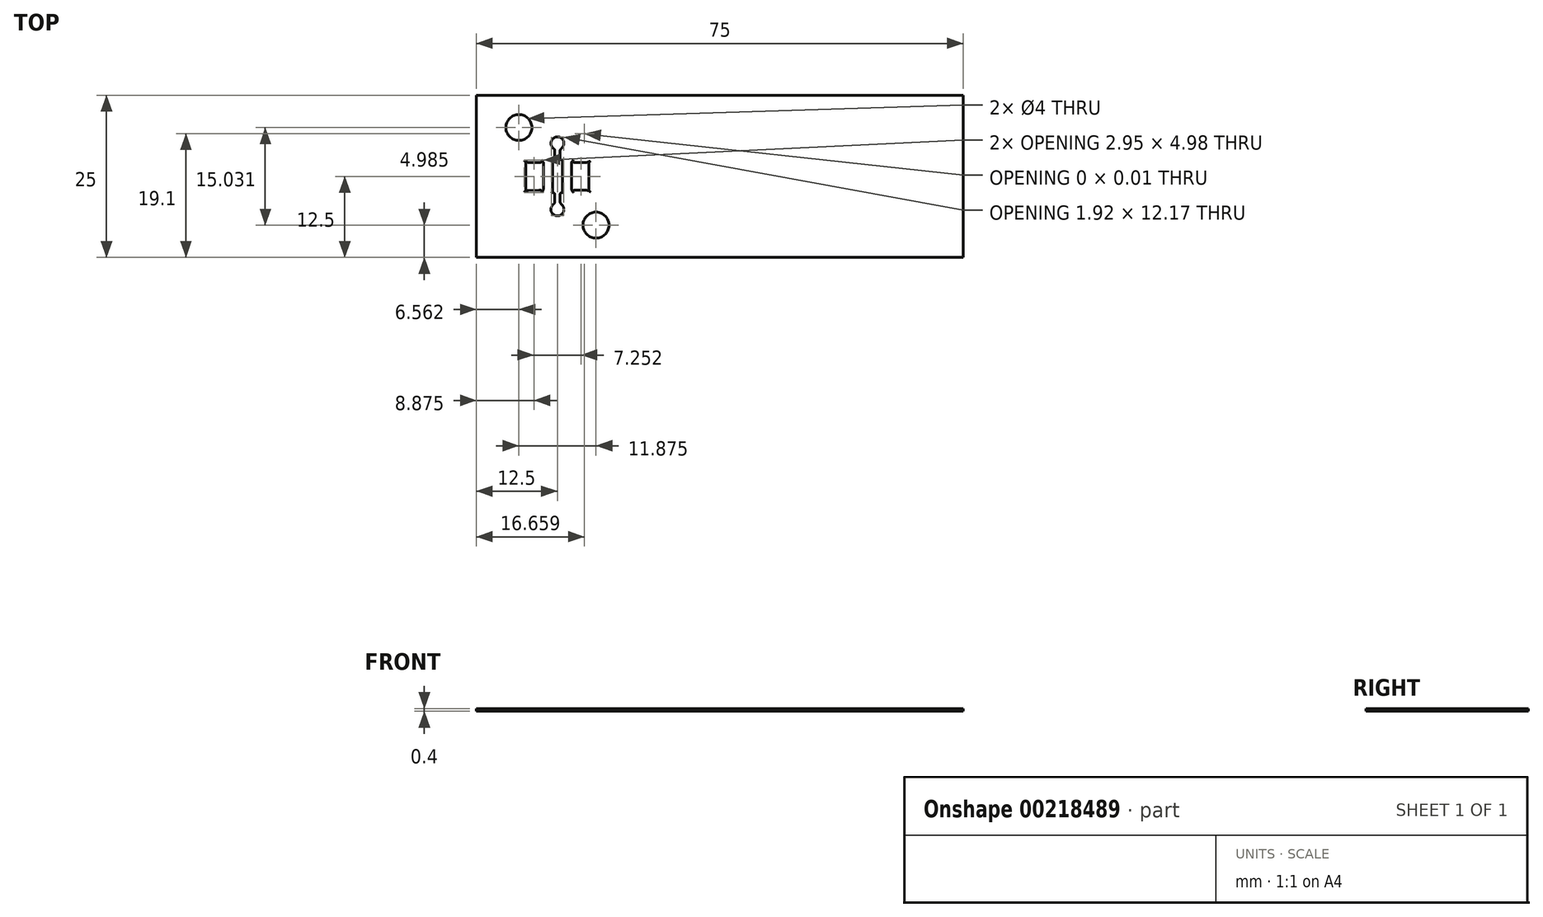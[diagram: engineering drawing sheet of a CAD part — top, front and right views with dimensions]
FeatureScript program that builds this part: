
annotation { "Feature Type Name" : "Feature", "Feature Type Description" : "" }
export const myFeature = defineFeature(function(context is Context, id is Id, definition is map)
    precondition{}
    {
        {
            var Q0;
            Q0=qCreatedBy(makeId("Top.planeOp"),FACE);
            var sketch = newSketch(context, id + "F0", { "sketchPlane" : qUnion([Q0])});
            skLineSegment(sketch, "E0.bottom", {"start": v(-37.5, 40) * mm, "end": v(37.5, 40) * mm});
            skLineSegment(sketch, "E0.top", {"start": v(-37.5, 15) * mm, "end": v(37.5, 15) * mm});
            skLineSegment(sketch, "E0.left", {"start": v(-37.5, 40) * mm, "end": v(-37.5, 15) * mm});
            skLineSegment(sketch, "E1.0", {"start": v(-37.5, 12.5) * mm, "end": v(37.5, 12.5) * mm});
            skLineSegment(sketch, "E2.top", {"start": v(-37.5, -12.5) * mm, "end": v(37.5, -12.5) * mm});
            skLineSegment(sketch, "E2.left", {"start": v(-37.5, 12.5) * mm, "end": v(-37.5, -12.5) * mm});
            skLineSegment(sketch, "E2.right", {"start": v(37.5, 12.5) * mm, "end": v(37.5, -12.5) * mm});
            skPoint(sketch, "E3.1.0.0", {"position": v(-17.06, 20.06) * mm});
            skPoint(sketch, "E3.1.0.4", {"position": v(-14.85, 26.8) * mm});
            skPoint(sketch, "E3.1.0.5", {"position": v(-25, 21.41) * mm});
            skLineSegment(sketch, "E3.1.0.10", {"start": v(-27.42, 30) * mm, "end": v(-29.86, 33.04) * mm});
            skPoint(sketch, "E3.1.0.11", {"position": v(-32.94, 20.06) * mm});
            skPoint(sketch, "E3.1.0.13", {"position": v(-25.75, 25) * mm});
            skPoint(sketch, "E3.1.0.15", {"position": v(-17.06, 34.94) * mm});
            skPoint(sketch, "E3.1.0.16", {"position": v(-24.49, 21.55) * mm});
            skLineSegment(sketch, "E3.1.0.17", {"start": v(-26.21, 24.92) * mm, "end": v(-29.12, 21.3) * mm});
            skLineSegment(sketch, "E3.1.0.19", {"start": v(-26.21, 30.08) * mm, "end": v(-29.1, 33.69) * mm});
            skLineSegment(sketch, "E3.1.0.20", {"start": v(-27.42, 25) * mm, "end": v(-29.87, 21.96) * mm});
            skPoint(sketch, "E3.1.0.24", {"position": v(-20.15, 29.65) * mm});
            skPoint(sketch, "E3.1.0.25", {"position": v(-22.85, 25.35) * mm});
            skPoint(sketch, "E3.1.0.27", {"position": v(-35.15, 26.8) * mm});
            skPoint(sketch, "E3.1.0.31", {"position": v(-27.15, 29.65) * mm});
            skPoint(sketch, "E3.1.0.35", {"position": v(-25.75, 30) * mm});
            skPoint(sketch, "E3.1.0.36", {"position": v(-27.15, 25.35) * mm});
            skPoint(sketch, "E3.1.0.41", {"position": v(-32.94, 34.94) * mm});
            skLineSegment(sketch, "E3.1.0.42", {"start": v(-23.79, 30.08) * mm, "end": v(-20.88, 33.7) * mm});
            skArc(sketch, "E3.1.0.43", {"start": v(-29.91, 29.7) * mm, "mid": v(-30, 29.78) * mm, "end": v(-30.1, 29.86) * mm});
            skArc(sketch, "E3.1.0.44", {"start": v(-20.08, 25.27) * mm, "mid": v(-14.77, 27.37) * mm, "end": v(-19.9, 29.89) * mm});
            skCircle(sketch, "E3.1.0.45", {"center": v(-19.06, 19.98) * mm, "radius": 2 * mm});
            skLineSegment(sketch, "E3.1.0.46", {"start": v(-23.79, 24.92) * mm, "end": v(-20.88, 21.3) * mm});
            skCircle(sketch, "E3.1.0.47", {"center": v(-30.94, 19.98) * mm, "radius": 2 * mm});
            skPoint(sketch, "E3.1.0.50", {"position": v(-25, 33.59) * mm});
            skLineSegment(sketch, "E3.1.0.60", {"start": v(-22.58, 25) * mm, "end": v(-20.13, 21.96) * mm});
            skPoint(sketch, "E3.1.0.61", {"position": v(-27.15, 25.35) * mm});
            skPoint(sketch, "E3.1.0.62", {"position": v(-27.15, 29.65) * mm});
            skPoint(sketch, "E3.1.0.64", {"position": v(-22.85, 25.35) * mm});
            skLineSegment(sketch, "E3.1.0.68", {"start": v(-22.58, 30) * mm, "end": v(-20.14, 33.04) * mm});
            skPoint(sketch, "E3.1.0.69", {"position": v(-27.15, 25.35) * mm});
            skPoint(sketch, "E3.1.0.72", {"position": v(-27.15, 29.65) * mm});
            skLineSegment(sketch, "E3.1.0.78", {"start": v(-29.85, 29.65) * mm, "end": v(-29.86, 29.65) * mm});
            skPoint(sketch, "E3.1.0.79", {"position": v(-22.85, 29.65) * mm});
            skPoint(sketch, "E3.1.0.81", {"position": v(-22.85, 25.35) * mm});
            skPoint(sketch, "E3.1.0.85", {"position": v(-22.85, 25.35) * mm});
            skPoint(sketch, "E3.1.0.87", {"position": v(-27.15, 25.35) * mm});
            skPoint(sketch, "E3.1.0.88", {"position": v(-27.15, 29.65) * mm});
            skLineSegment(sketch, "E3.1.0.89", {"start": v(-22.15, 29.65) * mm, "end": v(-20.49, 29.65) * mm});
            skPoint(sketch, "E3.1.0.90", {"position": v(-25, 27.5) * mm});
            skPoint(sketch, "E3.1.0.92", {"position": v(-22.85, 29.65) * mm});
            skPoint(sketch, "E3.1.0.95", {"position": v(-22.85, 25.35) * mm});
            skPoint(sketch, "E3.1.0.98", {"position": v(-27.15, 29.65) * mm});
            skPoint(sketch, "E3.1.0.99", {"position": v(-27.15, 25.35) * mm});
            skPoint(sketch, "E3.1.0.100", {"position": v(-22.85, 29.65) * mm});
            skLineSegment(sketch, "E3.1.0.104", {"start": v(-25.75, 25.21) * mm, "end": v(-25.75, 29.79) * mm});
            skLineSegment(sketch, "E3.1.0.105", {"start": v(-24.25, 29.79) * mm, "end": v(-24.25, 28.19) * mm});
            skLineSegment(sketch, "E3.1.0.106", {"start": v(-24.6, 24.7) * mm, "end": v(-24.6, 23.58) * mm});
            skLineSegment(sketch, "E3.1.0.108", {"start": v(-22.41, 29.65) * mm, "end": v(-22.15, 29.65) * mm});
            skLineSegment(sketch, "E3.1.0.109", {"start": v(-24.04, 30) * mm, "end": v(-23.95, 30) * mm});
            skLineSegment(sketch, "E3.1.0.110", {"start": v(-25.4, 30.5) * mm, "end": v(-25.4, 30.3) * mm});
            skArc(sketch, "E3.1.0.111", {"start": v(-24.6, 30.3) * mm, "mid": v(-24.51, 30.09) * mm, "end": v(-24.3, 30) * mm});
            skArc(sketch, "E3.1.0.112", {"start": v(-25.4, 30.3) * mm, "mid": v(-25.49, 30.09) * mm, "end": v(-25.7, 30) * mm});
            skLineSegment(sketch, "E3.1.0.113", {"start": v(-24.6, 30.3) * mm, "end": v(-24.6, 31.42) * mm});
            skLineSegment(sketch, "E3.1.0.115", {"start": v(-24.25, 30) * mm, "end": v(-24.3, 30) * mm});
            skLineSegment(sketch, "E3.1.0.117", {"start": v(-25.96, 30) * mm, "end": v(-26.05, 30) * mm});
            skLineSegment(sketch, "E3.1.0.118", {"start": v(-25.4, 24.7) * mm, "end": v(-25.4, 24.5) * mm});
            skLineSegment(sketch, "E3.1.0.120", {"start": v(-25.96, 25) * mm, "end": v(-26.05, 25) * mm});
            skArc(sketch, "E3.1.0.123", {"start": v(-25.4, 24.7) * mm, "mid": v(-25.49, 24.91) * mm, "end": v(-25.7, 25) * mm});
            skLineSegment(sketch, "E3.1.0.125", {"start": v(-24.25, 25) * mm, "end": v(-24.3, 25) * mm});
            skLineSegment(sketch, "E3.1.0.128", {"start": v(-24.04, 25) * mm, "end": v(-23.95, 25) * mm});
            skArc(sketch, "E3.1.0.134", {"start": v(-24.6, 24.7) * mm, "mid": v(-24.51, 24.91) * mm, "end": v(-24.3, 25) * mm});
            skLineSegment(sketch, "E3.1.0.151", {"start": v(-27.59, 25.35) * mm, "end": v(-27.85, 25.35) * mm});
            skLineSegment(sketch, "E4", {"start": v(-25.4, 24.5) * mm, "end": v(-25.4, 23.58) * mm});
            skLineSegment(sketch, "E5.top", {"start": v(-22.41, 25.35) * mm, "end": v(-20.5, 25.35) * mm});
            skLineSegment(sketch, "E5.left", {"start": v(-22.85, 29.44) * mm, "end": v(-22.85, 25.56) * mm});
            skLineSegment(sketch, "E5.right", {"start": v(-20.15, 29.57) * mm, "end": v(-20.15, 25.42) * mm});
            skLineSegment(sketch, "E6.left", {"start": v(-29.85, 29.55) * mm, "end": v(-29.85, 25.42) * mm});
            skLineSegment(sketch, "E6.right", {"start": v(-27.15, 29.44) * mm, "end": v(-27.15, 25.56) * mm});
            skLineSegment(sketch, "E7", {"start": v(-25.75, 25) * mm, "end": v(-25.7, 25) * mm});
            skLineSegment(sketch, "E8", {"start": v(-25.75, 30) * mm, "end": v(-25.7, 30) * mm});
            skLineSegment(sketch, "E9", {"start": v(-29.85, 25.35) * mm, "end": v(-29.85, 25.34) * mm});
            skArc(sketch, "E10.filletArc", {"start": v(-22.41, 25.35) * mm, "mid": v(-22.6, 25.23) * mm, "end": v(-22.58, 25) * mm});
            skPoint(sketch, "E11.visualSharp", {"position": v(-23.85, 25) * mm});
            skArc(sketch, "E11.filletArc", {"start": v(-23.79, 24.92) * mm, "mid": v(-23.86, 24.98) * mm, "end": v(-23.95, 25) * mm});
            skArc(sketch, "E12.filletArc", {"start": v(-22.58, 30) * mm, "mid": v(-22.6, 29.77) * mm, "end": v(-22.41, 29.65) * mm});
            skPoint(sketch, "E13.visualSharp", {"position": v(-23.85, 30) * mm});
            skArc(sketch, "E13.filletArc", {"start": v(-23.95, 30) * mm, "mid": v(-23.86, 30.02) * mm, "end": v(-23.79, 30.08) * mm});
            skPoint(sketch, "E14.visualSharp", {"position": v(-26.15, 30) * mm});
            skArc(sketch, "E14.filletArc", {"start": v(-26.21, 30.08) * mm, "mid": v(-26.14, 30.02) * mm, "end": v(-26.05, 30) * mm});
            skPoint(sketch, "E15.visualSharp", {"position": v(-26.15, 25) * mm});
            skArc(sketch, "E15.filletArc", {"start": v(-26.05, 25) * mm, "mid": v(-26.14, 24.98) * mm, "end": v(-26.21, 24.92) * mm});
            skArc(sketch, "E16", {"start": v(-27.42, 25) * mm, "mid": v(-27.26, 25.27) * mm, "end": v(-27.15, 25.56) * mm});
            skArc(sketch, "E17", {"start": v(-27.15, 29.44) * mm, "mid": v(-27.22, 29.75) * mm, "end": v(-27.42, 30) * mm});
            skArc(sketch, "E18", {"start": v(-27.59, 29.65) * mm, "mid": v(-27.43, 29.78) * mm, "end": v(-27.42, 30) * mm});
            skArc(sketch, "E19", {"start": v(-27.42, 25) * mm, "mid": v(-27.4, 25.23) * mm, "end": v(-27.59, 25.35) * mm});
            skArc(sketch, "E20.MirrorCS", {"start": v(-22.58, 25) * mm, "mid": v(-22.6, 25.23) * mm, "end": v(-22.41, 25.35) * mm});
            skArc(sketch, "E21.MirrorCS", {"start": v(-22.85, 29.44) * mm, "mid": v(-22.78, 29.75) * mm, "end": v(-22.58, 30) * mm});
            skArc(sketch, "E22.MirrorCS", {"start": v(-22.58, 25) * mm, "mid": v(-22.74, 25.27) * mm, "end": v(-22.85, 25.56) * mm});
            skLineSegment(sketch, "E23", {"start": v(-22.41, 29.65) * mm, "end": v(-20.49, 29.65) * mm});
            skArc(sketch, "E24", {"start": v(-19.9, 25.1) * mm, "mid": v(-20.18, 25.26) * mm, "end": v(-20.5, 25.35) * mm});
            skArc(sketch, "E25", {"start": v(-20.13, 21.96) * mm, "mid": v(-19.95, 21.86) * mm, "end": v(-19.75, 21.86) * mm});
            skArc(sketch, "E26", {"start": v(-20.85, 20.88) * mm, "mid": v(-20.81, 21.1) * mm, "end": v(-20.88, 21.3) * mm});
            skLineSegment(sketch, "E27", {"start": v(-24.6, 23.58) * mm, "end": v(-24.6, 23.58) * mm});
            skArc(sketch, "E28.MirrorCS", {"start": v(-29.87, 21.96) * mm, "mid": v(-30.05, 21.86) * mm, "end": v(-30.25, 21.86) * mm});
            skArc(sketch, "E29.MirrorCS", {"start": v(-29.15, 20.88) * mm, "mid": v(-29.19, 21.1) * mm, "end": v(-29.12, 21.3) * mm});
            skArc(sketch, "E30.MirrorCS", {"start": v(-25.4, 23.58) * mm, "mid": v(-25.46, 23.37) * mm, "end": v(-25.61, 23.2) * mm});
            skArc(sketch, "E31", {"start": v(-24.6, 23.58) * mm, "mid": v(-24.54, 23.37) * mm, "end": v(-24.39, 23.2) * mm});
            skArc(sketch, "E32", {"start": v(-25.61, 23.2) * mm, "mid": v(-25, 21.41) * mm, "end": v(-24.39, 23.2) * mm});
            skLineSegment(sketch, "E33", {"start": v(-29.12, 21.3) * mm, "end": v(-29.12, 21.3) * mm});
            skLineSegment(sketch, "E34", {"start": v(-29.5, 25.34) * mm, "end": v(-27.85, 25.35) * mm});
            skArc(sketch, "E35.filletArc", {"start": v(-29.91, 25.27) * mm, "mid": v(-29.87, 25.34) * mm, "end": v(-29.85, 25.42) * mm});
            skArc(sketch, "E36.filletArc", {"start": v(-29.85, 29.55) * mm, "mid": v(-29.87, 29.63) * mm, "end": v(-29.91, 29.7) * mm});
            skLineSegment(sketch, "E37", {"start": v(-29.5, 29.65) * mm, "end": v(-27.59, 29.65) * mm});
            skArc(sketch, "E38", {"start": v(-30.1, 29.86) * mm, "mid": v(-35.1, 27.5) * mm, "end": v(-30.1, 25.1) * mm});
            skArc(sketch, "E39", {"start": v(-30.1, 29.86) * mm, "mid": v(-29.8, 29.72) * mm, "end": v(-29.5, 29.65) * mm});
            skArc(sketch, "E40", {"start": v(-30.27, 33.13) * mm, "mid": v(-32.26, 36.51) * mm, "end": v(-29.15, 34.12) * mm});
            skArc(sketch, "E41", {"start": v(-30.02, 33.24) * mm, "mid": v(-30.14, 33.18) * mm, "end": v(-30.27, 33.13) * mm});
            skArc(sketch, "E42", {"start": v(-29.15, 34.12) * mm, "mid": v(-29.52, 33.6) * mm, "end": v(-30.02, 33.24) * mm});
            skArc(sketch, "E43", {"start": v(-29.86, 33.04) * mm, "mid": v(-30.05, 33.13) * mm, "end": v(-30.27, 33.13) * mm});
            skArc(sketch, "E44", {"start": v(-29.15, 34.12) * mm, "mid": v(-29.19, 33.9) * mm, "end": v(-29.1, 33.69) * mm});
            skLineSegment(sketch, "E45", {"start": v(-25.4, 31.67) * mm, "end": v(-25.4, 31.67) * mm});
            skLineSegment(sketch, "E46", {"start": v(-25.4, 31.42) * mm, "end": v(-25.4, 30.5) * mm});
            skArc(sketch, "E47", {"start": v(-25.4, 31.42) * mm, "mid": v(-25.46, 31.64) * mm, "end": v(-25.62, 31.8) * mm});
            skArc(sketch, "E48", {"start": v(-24.38, 31.8) * mm, "mid": v(-25, 33.59) * mm, "end": v(-25.62, 31.8) * mm});
            skArc(sketch, "E49", {"start": v(-24.38, 31.8) * mm, "mid": v(-24.53, 31.64) * mm, "end": v(-24.6, 31.42) * mm});
            skArc(sketch, "E50.filletArc", {"start": v(-25.75, 29.79) * mm, "mid": v(-25.81, 29.94) * mm, "end": v(-25.96, 30) * mm});
            skLineSegment(sketch, "E51", {"start": v(-25.96, 30) * mm, "end": v(-25.75, 30) * mm});
            skPoint(sketch, "E52.visualSharp", {"position": v(-24.25, 30) * mm});
            skArc(sketch, "E52.filletArc", {"start": v(-24.04, 30) * mm, "mid": v(-24.19, 29.94) * mm, "end": v(-24.25, 29.79) * mm});
            skLineSegment(sketch, "E53", {"start": v(-24.25, 30) * mm, "end": v(-24.04, 30) * mm});
            skArc(sketch, "E54", {"start": v(-20.84, 34.1) * mm, "mid": v(-20.79, 34) * mm, "end": v(-20.72, 33.9) * mm});
            skArc(sketch, "E55", {"start": v(-20.72, 33.9) * mm, "mid": v(-20.4, 33.52) * mm, "end": v(-19.98, 33.24) * mm});
            skArc(sketch, "E56", {"start": v(-20.88, 33.7) * mm, "mid": v(-20.8, 33.9) * mm, "end": v(-20.84, 34.1) * mm});
            skArc(sketch, "E57", {"start": v(-19.73, 33.13) * mm, "mid": v(-17.75, 36.52) * mm, "end": v(-20.84, 34.1) * mm});
            skArc(sketch, "E58", {"start": v(-19.98, 33.24) * mm, "mid": v(-19.86, 33.18) * mm, "end": v(-19.73, 33.13) * mm});
            skArc(sketch, "E59", {"start": v(-19.73, 33.13) * mm, "mid": v(-19.94, 33.13) * mm, "end": v(-20.14, 33.04) * mm});
            skArc(sketch, "E60", {"start": v(-19.9, 29.89) * mm, "mid": v(-20, 29.8) * mm, "end": v(-20.08, 29.72) * mm});
            skLineSegment(sketch, "E61", {"start": v(-20.15, 29.65) * mm, "end": v(-20.15, 29.65) * mm});
            skArc(sketch, "E62", {"start": v(-20.49, 29.65) * mm, "mid": v(-20.18, 29.74) * mm, "end": v(-19.9, 29.89) * mm});
            skArc(sketch, "E63.filletArc", {"start": v(-20.08, 29.72) * mm, "mid": v(-20.13, 29.65) * mm, "end": v(-20.15, 29.57) * mm});
            skArc(sketch, "E64.filletArc", {"start": v(-20.15, 25.42) * mm, "mid": v(-20.13, 25.34) * mm, "end": v(-20.08, 25.27) * mm});
            skPoint(sketch, "E65.visualSharp", {"position": v(-24.25, 25) * mm});
            skArc(sketch, "E65.filletArc", {"start": v(-24.25, 25.21) * mm, "mid": v(-24.19, 25.06) * mm, "end": v(-24.04, 25) * mm});
            skLineSegment(sketch, "E66", {"start": v(-24.25, 25) * mm, "end": v(-24.04, 25) * mm});
            skLineSegment(sketch, "E67", {"start": v(-24.25, 25.21) * mm, "end": v(-24.25, 26.81) * mm});
            skArc(sketch, "E68.filletArc", {"start": v(-25.96, 25) * mm, "mid": v(-25.81, 25.06) * mm, "end": v(-25.75, 25.21) * mm});
            skLineSegment(sketch, "E69", {"start": v(-25.96, 25) * mm, "end": v(-25.75, 25) * mm});
            skArc(sketch, "E70", {"start": v(-30.1, 25.1) * mm, "mid": v(-30, 25.19) * mm, "end": v(-29.91, 25.27) * mm});
            skLineSegment(sketch, "E71", {"start": v(-29.91, 25.27) * mm, "end": v(-29.91, 25.27) * mm});
            skArc(sketch, "E72", {"start": v(-29.5, 25.34) * mm, "mid": v(-29.82, 25.26) * mm, "end": v(-30.1, 25.1) * mm});
            skLineSegment(sketch, "E73", {"start": v(-25, 32.59) * mm, "end": v(-25, 22.41) * mm});
            skPoint(sketch, "E74.endSnap0", {"position": v(-24.25, 27.5) * mm});
            skLineSegment(sketch, "E75", {"start": v(-24.72, 27.46) * mm, "end": v(-24.34, 26.96) * mm});
            skPoint(sketch, "E76.newPointB", {"position": v(-24.25, 25.21) * mm});
            skPoint(sketch, "E77.visualSharp", {"position": v(-24.75, 27.5) * mm});
            skArc(sketch, "E77.filletArc", {"start": v(-24.72, 27.54) * mm, "mid": v(-24.73, 27.52) * mm, "end": v(-24.73, 27.5) * mm});
            skArc(sketch, "E78.filletArc", {"start": v(-24.34, 26.96) * mm, "mid": v(-24.28, 26.94) * mm, "end": v(-24.25, 26.99) * mm});
            skLineSegment(sketch, "E79", {"start": v(-24.25, 27.5) * mm, "end": v(-24.25, 26.99) * mm});
            skArc(sketch, "E80", {"start": v(-24.73, 27.5) * mm, "mid": v(-24.73, 27.48) * mm, "end": v(-24.72, 27.46) * mm});
            skLineSegment(sketch, "E81.MirrorCS", {"start": v(-24.72, 27.54) * mm, "end": v(-24.34, 28.04) * mm});
            skArc(sketch, "E82.MirrorCS", {"start": v(-24.34, 28.04) * mm, "mid": v(-24.28, 28.06) * mm, "end": v(-24.25, 28.01) * mm});
            skLineSegment(sketch, "E83.MirrorCS", {"start": v(-24.25, 27.5) * mm, "end": v(-24.25, 28.01) * mm});
            skLineSegment(sketch, "E84", {"start": v(-24.25, 26.81) * mm, "end": v(-24.25, 26.99) * mm});
            skLineSegment(sketch, "E85", {"start": v(-24.25, 28.19) * mm, "end": v(-24.25, 28.01) * mm});
            skLineSegment(sketch, "E86.MirrorCS", {"start": v(-25.28, 27.54) * mm, "end": v(-25.66, 28.04) * mm});
            skArc(sketch, "E87.MirrorCS", {"start": v(-25.66, 28.04) * mm, "mid": v(-25.72, 28.06) * mm, "end": v(-25.75, 28.01) * mm});
            skArc(sketch, "E88.MirrorCS", {"start": v(-25.28, 27.54) * mm, "mid": v(-25.27, 27.52) * mm, "end": v(-25.27, 27.5) * mm});
            skArc(sketch, "E89.MirrorCS", {"start": v(-25.27, 27.5) * mm, "mid": v(-25.27, 27.48) * mm, "end": v(-25.28, 27.46) * mm});
            skLineSegment(sketch, "E90.MirrorCS", {"start": v(-25.28, 27.46) * mm, "end": v(-25.66, 26.96) * mm});
            skArc(sketch, "E91.MirrorCS", {"start": v(-25.66, 26.96) * mm, "mid": v(-25.72, 26.94) * mm, "end": v(-25.75, 26.99) * mm});
            skCircle(sketch, "E92", {"center": v(0, 13.86) * mm, "radius": 50 * mm});
            skLineSegment(sketch, "E93", {"start": v(37.5, 40) * mm, "end": v(37.5, 15) * mm});
            skSolve(sketch);
        }
        {
            var Q0;
            {var subQ1=sQuery(id+"F0.wireOp",EDGE,"E3.1.0.42");Q0=makeQuery(id+"F0.imprint","IMPRINT",FACE,{"disambiguationData":[TD([[makeQuery(id+"F0.imprint","IMPRINT",EDGE,{"derivedFrom":subQ1}),-1.0]])]});}
            var Q1;
            Q1=makeQuery(id+"F0.imprint","IMPRINT",FACE,{"disambiguationData":[TD([[makeQuery(id+"F0.imprint","IMPRINT",EDGE,{"derivedFrom":sQuery(id+"F0.wireOp",EDGE,"E3.1.0.10")}),-1.0]])]});
            var Q2;
            Q2=makeQuery(id+"F0.imprint","IMPRINT",FACE,{"disambiguationData":[TD([[makeQuery(id+"F0.imprint","IMPRINT",EDGE,{"derivedFrom":sQuery(id+"F0.wireOp",EDGE,"E40")}),-1.0]])]});
            var Q3;
            {var subQ4=sQuery(id+"F0.wireOp",EDGE,"E55");Q3=makeQuery(id+"F0.imprint","IMPRINT",FACE,{"disambiguationData":[TD([[makeQuery(id+"F0.imprint","IMPRINT",EDGE,{"derivedFrom":subQ4}),1.0]])]});}
            var Q4;
            Q4=makeQuery(id+"F0.imprint","IMPRINT",FACE,{"disambiguationData":[TD([[makeQuery(id+"F0.imprint","IMPRINT",EDGE,{"derivedFrom":sQuery(id+"F0.wireOp",EDGE,"E5.right")}),1.0]])]});
            var Q5;
            {var subQ0=sQuery(id+"F0.wireOp",EDGE,"E3.1.0.45");var subQ1=makeQuery(id+"F0.imprint","INTERSECT",VERTEX,{"derivedFrom":[subQ0,sQuery(id+"F0.wireOp",EDGE,"E25")]});Q5=makeQuery(id+"F0.imprint","IMPRINT",FACE,{"disambiguationData":[TD([[makeQuery(id+"F0.imprint","IMPRINT",EDGE,{"disambiguationData":[TD([[subQ1,1.0]])],"derivedFrom":subQ0}),-1.0]])]});}
            var Q6;
            {var subQ0=sQuery(id+"F0.wireOp",EDGE,"E3.1.0.47");var subQ1=makeQuery(id+"F0.imprint","INTERSECT",VERTEX,{"derivedFrom":[subQ0,sQuery(id+"F0.wireOp",EDGE,"E28.MirrorCS")]});Q6=makeQuery(id+"F0.imprint","IMPRINT",FACE,{"disambiguationData":[TD([[makeQuery(id+"F0.imprint","IMPRINT",EDGE,{"disambiguationData":[TD([[subQ1,1.0]])],"derivedFrom":subQ0}),1.0]])]});}
            var Q7;
            Q7=makeQuery(id+"F0.imprint","IMPRINT",FACE,{"disambiguationData":[TD([[makeQuery(id+"F0.imprint","IMPRINT",EDGE,{"derivedFrom":sQuery(id+"F0.wireOp",EDGE,"E3.1.0.43")}),1.0]])]});
            extrude(context, id + "F1", {"entities" : qUnion([Q0, Q1, Q2, Q3, Q4, Q5, Q6, Q7]), "depth" : .4 * mm});
        }
    });
